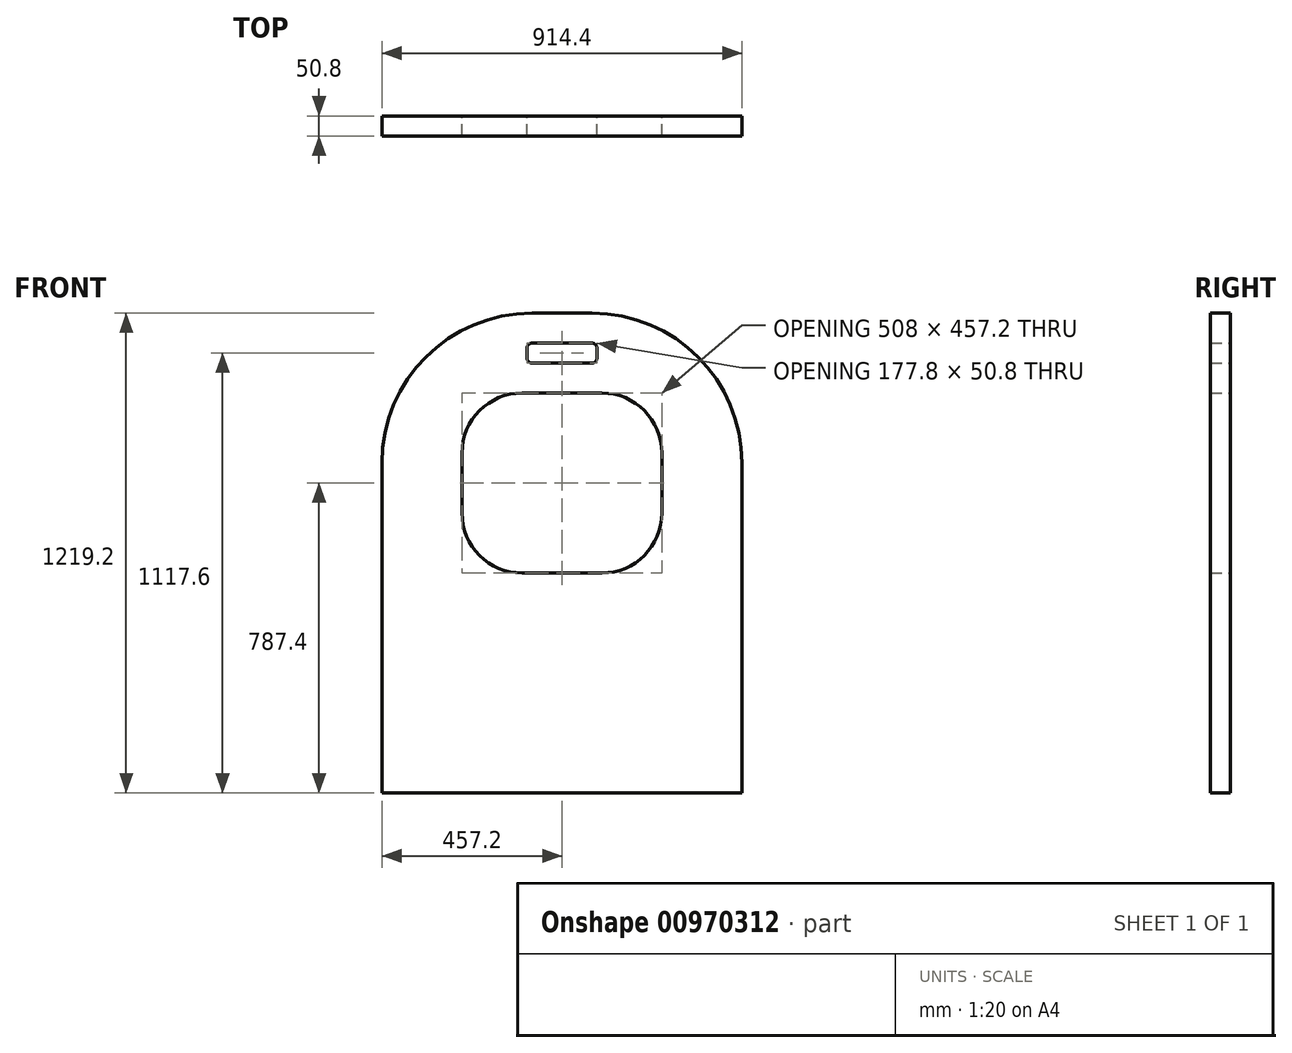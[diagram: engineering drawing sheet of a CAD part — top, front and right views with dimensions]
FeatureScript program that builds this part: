
annotation { "Feature Type Name" : "Feature", "Feature Type Description" : "" }
export const myFeature = defineFeature(function(context is Context, id is Id, definition is map)
    precondition{}
    {
        {
            var Q0;
            Q0=qCreatedBy(makeId("Front.planeOp"),FACE);
            var sketch = newSketch(context, id + "F0", { "sketchPlane" : qUnion([Q0])});
            skLineSegment(sketch, "E0.bottom", {"start": v(-457.2, 0) * mm, "end": v(457.2, 0) * mm});
            skLineSegment(sketch, "E0.top", {"start": v(-76.2, 1219.2) * mm, "end": v(76.2, 1219.2) * mm});
            skLineSegment(sketch, "E0.left", {"start": v(-457.2, 0) * mm, "end": v(-457.2, 838.2) * mm});
            skLineSegment(sketch, "E0.right", {"start": v(457.2, 0) * mm, "end": v(457.2, 838.2) * mm});
            skPoint(sketch, "E1.visualSharp", {"position": v(-457.2, 1219.2) * mm});
            skArc(sketch, "E1.filletArc", {"start": v(-76.2, 1219.2) * mm, "mid": v(-345.6, 1107.6) * mm, "end": v(-457.2, 838.2) * mm});
            skPoint(sketch, "E2.visualSharp", {"position": v(457.2, 1219.2) * mm});
            skArc(sketch, "E2.filletArc", {"start": v(457.2, 838.2) * mm, "mid": v(345.6, 1107.6) * mm, "end": v(76.2, 1219.2) * mm});
            skLineSegment(sketch, "E3.bottom", {"start": v(101.6, 558.8) * mm, "end": v(-101.6, 558.8) * mm});
            skLineSegment(sketch, "E3.top", {"start": v(101.6, 1016) * mm, "end": v(-101.6, 1016) * mm});
            skLineSegment(sketch, "E3.left", {"start": v(254, 711.2) * mm, "end": v(254, 863.6) * mm});
            skLineSegment(sketch, "E3.right", {"start": v(-254, 711.2) * mm, "end": v(-254, 863.6) * mm});
            skPoint(sketch, "E4.visualSharp", {"position": v(-254, 1016) * mm});
            skArc(sketch, "E4.filletArc", {"start": v(-101.6, 1016) * mm, "mid": v(-209.36, 971.36) * mm, "end": v(-254, 863.6) * mm});
            skPoint(sketch, "E5.visualSharp", {"position": v(254, 1016) * mm});
            skArc(sketch, "E5.filletArc", {"start": v(254, 863.6) * mm, "mid": v(209.36, 971.36) * mm, "end": v(101.6, 1016) * mm});
            skPoint(sketch, "E6.visualSharp", {"position": v(-254, 558.8) * mm});
            skArc(sketch, "E6.filletArc", {"start": v(-254, 711.2) * mm, "mid": v(-209.36, 603.44) * mm, "end": v(-101.6, 558.8) * mm});
            skPoint(sketch, "E7.visualSharp", {"position": v(254, 558.8) * mm});
            skArc(sketch, "E7.filletArc", {"start": v(101.6, 558.8) * mm, "mid": v(209.36, 603.44) * mm, "end": v(254, 711.2) * mm});
            skLineSegment(sketch, "E8.bottom", {"start": v(-76.2, 1092.2) * mm, "end": v(76.2, 1092.2) * mm});
            skLineSegment(sketch, "E8.top", {"start": v(-76.2, 1143) * mm, "end": v(76.2, 1143) * mm});
            skLineSegment(sketch, "E8.left", {"start": v(-88.9, 1104.9) * mm, "end": v(-88.9, 1130.3) * mm});
            skLineSegment(sketch, "E8.right", {"start": v(88.9, 1104.9) * mm, "end": v(88.9, 1130.3) * mm});
            skPoint(sketch, "E9.visualSharp", {"position": v(-88.9, 1143) * mm});
            skArc(sketch, "E9.filletArc", {"start": v(-76.2, 1143) * mm, "mid": v(-85.18, 1139.28) * mm, "end": v(-88.9, 1130.3) * mm});
            skPoint(sketch, "E10.visualSharp", {"position": v(-88.9, 1092.2) * mm});
            skArc(sketch, "E10.filletArc", {"start": v(-88.9, 1104.9) * mm, "mid": v(-85.18, 1095.92) * mm, "end": v(-76.2, 1092.2) * mm});
            skPoint(sketch, "E11.visualSharp", {"position": v(88.9, 1092.2) * mm});
            skArc(sketch, "E11.filletArc", {"start": v(76.2, 1092.2) * mm, "mid": v(85.18, 1095.92) * mm, "end": v(88.9, 1104.9) * mm});
            skPoint(sketch, "E12.visualSharp", {"position": v(88.9, 1143) * mm});
            skArc(sketch, "E12.filletArc", {"start": v(88.9, 1130.3) * mm, "mid": v(85.18, 1139.28) * mm, "end": v(76.2, 1143) * mm});
            skSolve(sketch);
        }
        {
            var Q0;
            Q0=makeQuery(id+"F0.imprint","IMPRINT",FACE,{"disambiguationData":[TD([[makeQuery(id+"F0.imprint","IMPRINT",EDGE,{"derivedFrom":sQuery(id+"F0.wireOp",EDGE,"E0.bottom")}),1.0]])]});
            extrude(context, id + "F1", {"entities" : qUnion([Q0]), "depth" : 50.8 * mm, "offsetDistance" : 25.4 * mm, "symmetric" : true});
        }
    });
